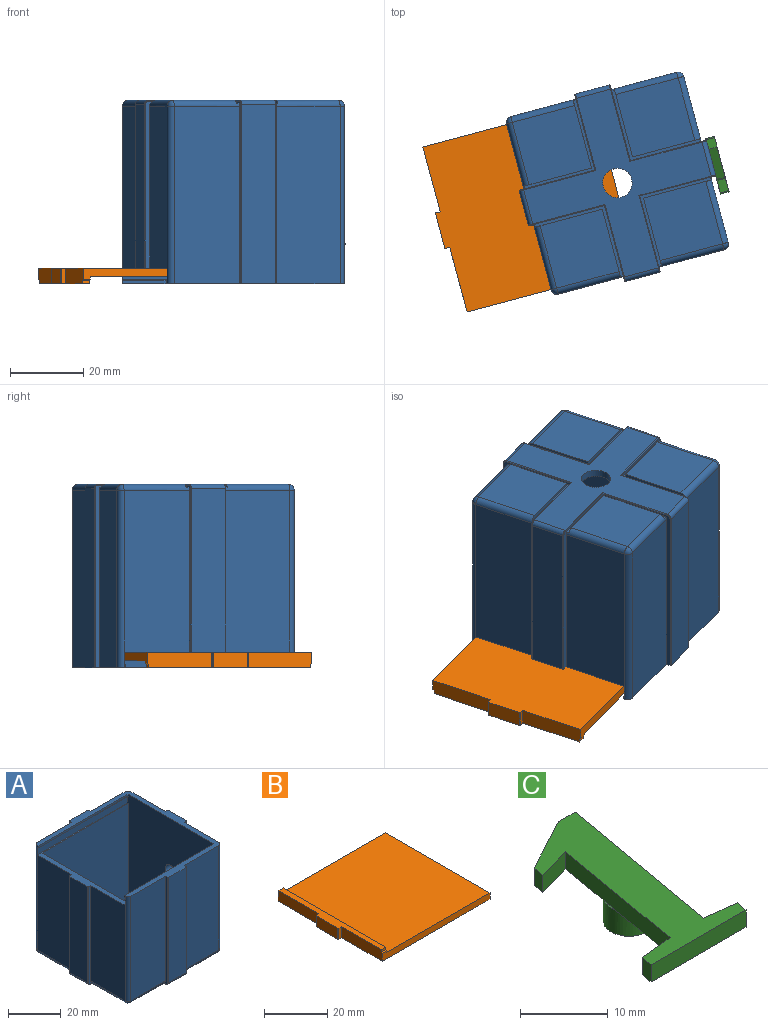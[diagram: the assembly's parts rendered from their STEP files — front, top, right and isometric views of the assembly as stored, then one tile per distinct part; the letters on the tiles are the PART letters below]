
ASSEMBLY  parts=3 mates=2
PART A: 98 faces, bbox 53x53x50.1 mm
  f0: plane 1.27x0.4mm, normal (-1,0,0), area 0.4mm2, adj f6,f33,f62,f95
  f1: plane 1.27x0.4mm, normal (-1,0,0), area 0.4mm2, adj f6,f32,f58,f96
  f2: plane 44.13x18.4mm, normal (-1,0,0), area 812mm2, adj f3,f54,f55,f58
  f3: plane 45.53x21.2mm, normal (0,1,0), area 66.5mm2, adj f2,f30,f38,f54,f55,f73,f75,f76
  f4: plane 44.53x9.6mm, normal (-1,0,0), area 427.5mm2, adj f50,f54,f73,f79
  f5: plane 45.53x21.2mm, normal (0,-1,0), area 66.5mm2, adj f17,f19,f44,f54,f60,f79,f81,f82
  f6: plane 52.8x51.4mm, normal (0,0,1), area 331.8mm2, adj f0,f1,f14,f15,f18,f19,f20,f21
  f7: plane 46x43.73mm, normal (0,-1,0), area 2011.7mm2, adj f8,f34,f35,f54
  f8: plane 46x43.73mm, normal (1,0,0), area 2011.7mm2, adj f7,f9,f35,f54
  f9: plane 46x43.73mm, normal (0,1,0), area 2011.7mm2, adj f8,f34,f35,f54
  f10: plane 17.6x17.6mm, normal (0,0,-1), area 309.8mm2, adj f45,f46,f67,f68
  f11: plane 50.4x50.4mm, normal (0,0,-1), area 825.3mm2, adj f16,f48,f49,f50,f51,f74,f76,f80
  f12: plane 17.6x17.6mm, normal (0,0,-1), area 309.8mm2, adj f42,f43,f59,f60
  f13: plane 17.6x17.6mm, normal (0,0,-1), area 309.8mm2, adj f36,f37,f55,f56
  f14: plane 48.4x18.4mm, normal (1,0,0), area 890.6mm2, adj f6,f26,f68,f70
  f15: plane 48.4x18.4mm, normal (0,1,0), area 890.6mm2, adj f6,f30,f56,f58
  f16: cylinder r=4mm len=8mm, axis (0,0,-1), area 50.3mm2, adj f11,f35
  f17: plane 44.13x18.4mm, normal (-1,0,0), area 812mm2, adj f5,f54,f60,f62
  f18: plane 48.4x18.4mm, normal (0,-1,0), area 890.6mm2, adj f6,f19,f59,f62
  f19: plane 49.8x21.2mm, normal (-1,0,0), area 71.6mm2, adj f5,f6,f18,f44,f59,f77,f78,f80
  f20: plane 48.8x9.6mm, normal (0,-1,0), area 468.5mm2, adj f6,f49,f77,f85
  f21: plane 49.8x21.2mm, normal (1,0,0), area 71.6mm2, adj f6,f22,f24,f41,f64,f85,f87,f88
  f22: plane 48.4x18.4mm, normal (0,-1,0), area 890.6mm2, adj f6,f21,f64,f66
  f23: plane 48.4x18.4mm, normal (1,0,0), area 890.6mm2, adj f6,f24,f63,f66
  f24: plane 49.8x21.2mm, normal (0,-1,0), area 71.6mm2, adj f6,f21,f23,f41,f63,f83,f84,f86
  f25: plane 48.8x9.6mm, normal (1,0,0), area 440.2mm2, adj f6,f48,f83,f89,f97
  f26: plane 49.8x21.2mm, normal (0,1,0), area 71.6mm2, adj f6,f14,f28,f47,f68,f89,f90,f91
  f27: plane 48.4x18.4mm, normal (0,1,0), area 890.6mm2, adj f6,f28,f67,f70
  f28: plane 49.8x21.2mm, normal (1,0,0), area 71.6mm2, adj f6,f26,f27,f47,f67,f92,f93,f94
  f29: plane 48.8x9.6mm, normal (0,1,0), area 468.5mm2, adj f6,f51,f71,f93
  f30: plane 49.8x21.2mm, normal (-1,0,0), area 71.6mm2, adj f3,f6,f15,f38,f56,f71,f72,f74
  f31: plane 17.6x17.6mm, normal (0,0,-1), area 309.8mm2, adj f39,f40,f63,f64
  f32: plane 48x0.87mm, normal (0,-1,0), area 41.7mm2, adj f1,f6,f34,f96
  f33: plane 48x0.87mm, normal (0,1,0), area 41.7mm2, adj f0,f6,f34,f95
  f34: plane 48x46.8mm, normal (-1,0,0), area 2182.3mm2, adj f6,f7,f9,f32,f33,f35,f52,f53
  f35: plane 46x46mm, normal (0,0,1), area 2065.7mm2, adj f7,f8,f9,f16,f34
  f36: plane 18.99x0.8mm, normal (0,-1,0), area 14.9mm2, adj f13,f37,f38,f55
  f37: plane 18.99x0.8mm, normal (1,0,0), area 14.9mm2, adj f13,f36,f38,f56
  f38: plane 19.79x19.79mm, normal (0,0,-1), area 31mm2, adj f3,f30,f36,f37,f55,f56
  f39: plane 18.99x0.8mm, normal (-1,0,0), area 14.9mm2, adj f31,f40,f41,f64
  f40: plane 18.99x0.8mm, normal (0,1,0), area 14.9mm2, adj f31,f39,f41,f63
  f41: plane 19.79x19.79mm, normal (0,0,-1), area 31mm2, adj f21,f24,f39,f40,f63,f64
  f42: plane 18.99x0.8mm, normal (1,0,0), area 14.9mm2, adj f12,f43,f44,f59
  f43: plane 18.99x0.8mm, normal (0,1,0), area 14.9mm2, adj f12,f42,f44,f60
  f44: plane 19.79x19.79mm, normal (0,0,-1), area 31mm2, adj f5,f19,f42,f43,f59,f60
  f45: plane 18.99x0.8mm, normal (0,-1,0), area 14.9mm2, adj f10,f46,f47,f68
  f46: plane 18.99x0.8mm, normal (-1,0,0), area 14.9mm2, adj f10,f45,f47,f67
  f47: plane 19.79x19.79mm, normal (0,0,-1), area 31mm2, adj f26,f28,f45,f46,f67,f68
  f48: cylinder r=1.2mm len=9.6mm, axis (0,1,0), area 18.1mm2, adj f11,f25,f84,f90
  f49: cylinder r=1.2mm len=9.6mm, axis (1,0,0), area 18.1mm2, adj f11,f20,f78,f87
  f50: cylinder r=1.2mm len=9.6mm, axis (0,-1,0), area 18.1mm2, adj f4,f11,f75,f81
  f51: cylinder r=1.2mm len=9.6mm, axis (-1,0,0), area 18.1mm2, adj f11,f29,f72,f94
  f52: plane 48x3mm, normal (0,-1,0), area 144mm2, adj f34,f54,f58,f96
  f53: plane 48x3mm, normal (0,1,0), area 144mm2, adj f34,f54,f62,f95
  f54: plane 49.4x46.8mm, normal (0,0,1), area 144.4mm2, adj f2,f3,f4,f5,f7,f8,f9,f17
  f55: cylinder r=1.6mm len=18.4mm, axis (0,-1,0), area 44.9mm2, adj f2,f3,f13,f36,f38,f57
  f56: cylinder r=1.6mm len=18.4mm, axis (-1,0,0), area 44.9mm2, adj f13,f15,f30,f37,f38,f57
  f57: sphere r=1.6mm, area 4mm2, adj f55,f56,f58
  f58: cylinder r=1.6mm len=48.4mm, axis (0,0,1), area 121.6mm2, adj f1,f2,f6,f15,f52,f57
  f59: cylinder r=1.6mm len=18.4mm, axis (1,0,0), area 44.9mm2, adj f12,f18,f19,f42,f44,f61
  f60: cylinder r=1.6mm len=18.4mm, axis (0,-1,0), area 44.9mm2, adj f5,f12,f17,f43,f44,f61
  f61: sphere r=1.6mm, area 4mm2, adj f59,f60,f62
  f62: cylinder r=1.6mm len=48.4mm, axis (0,0,-1), area 121.6mm2, adj f0,f6,f17,f18,f53,f61
  f63: cylinder r=1.6mm len=18.4mm, axis (0,1,0), area 44.9mm2, adj f23,f24,f31,f40,f41,f65
  f64: cylinder r=1.6mm len=18.4mm, axis (1,0,0), area 44.9mm2, adj f21,f22,f31,f39,f41,f65
  f65: sphere r=1.6mm, area 4mm2, adj f63,f64,f66
  f66: cylinder r=1.6mm len=48.4mm, axis (0,0,1), area 121.6mm2, adj f6,f22,f23,f65
  f67: cylinder r=1.6mm len=18.4mm, axis (-1,0,0), area 44.9mm2, adj f10,f27,f28,f46,f47,f69
  f68: cylinder r=1.6mm len=18.4mm, axis (0,1,0), area 44.9mm2, adj f10,f14,f26,f45,f47,f69
  f69: sphere r=1.6mm, area 4mm2, adj f67,f68,f70
  f70: cylinder r=1.6mm len=48.4mm, axis (0,0,-1), area 121.6mm2, adj f6,f14,f27,f69
  f71: cylinder r=0.2mm len=48.8mm, axis (0,0,1), area 15.3mm2, adj f6,f29,f30,f72
  f72: torus R=1mm, axis (-1,0,0), area 0.6mm2, adj f30,f51,f71,f74
  f73: cylinder r=0.2mm len=44.53mm, axis (0,0,-1), area 14mm2, adj f3,f4,f54,f75
  f74: cylinder r=0.2mm len=20.4mm, axis (0,-1,0), area 6.4mm2, adj f11,f30,f72,f76
  f75: torus R=1mm, axis (0,-1,0), area 0.6mm2, adj f3,f50,f73,f76
  f76: cylinder r=0.2mm len=20.4mm, axis (-1,0,0), area 6.4mm2, adj f3,f11,f74,f75
  f77: cylinder r=0.2mm len=48.8mm, axis (0,0,-1), area 15.3mm2, adj f6,f19,f20,f78
  f78: torus R=1mm, axis (1,0,0), area 0.6mm2, adj f19,f49,f77,f80
  f79: cylinder r=0.2mm len=44.53mm, axis (0,0,1), area 14mm2, adj f4,f5,f54,f81
  f80: cylinder r=0.2mm len=20.4mm, axis (0,-1,0), area 6.4mm2, adj f11,f19,f78,f82
  f81: torus R=1mm, axis (0,-1,0), area 0.6mm2, adj f5,f50,f79,f82
  f82: cylinder r=0.2mm len=20.4mm, axis (1,0,0), area 6.4mm2, adj f5,f11,f80,f81
  f83: cylinder r=0.2mm len=48.8mm, axis (0,0,-1), area 15.3mm2, adj f6,f24,f25,f84
  f84: torus R=1mm, axis (0,1,0), area 0.6mm2, adj f24,f48,f83,f86
  f85: cylinder r=0.2mm len=48.8mm, axis (0,0,1), area 15.3mm2, adj f6,f20,f21,f87
  f86: cylinder r=0.2mm len=20.4mm, axis (1,0,0), area 6.4mm2, adj f11,f24,f84,f88
  f87: torus R=1mm, axis (1,0,0), area 0.6mm2, adj f21,f49,f85,f88
  f88: cylinder r=0.2mm len=20.4mm, axis (0,1,0), area 6.4mm2, adj f11,f21,f86,f87
  f89: cylinder r=0.2mm len=48.8mm, axis (0,0,1), area 15.3mm2, adj f6,f25,f26,f90
  f90: torus R=1mm, axis (0,1,0), area 0.6mm2, adj f26,f48,f89,f91
  f91: cylinder r=0.2mm len=20.4mm, axis (-1,0,0), area 6.4mm2, adj f11,f26,f90,f92
  f92: cylinder r=0.2mm len=20.4mm, axis (0,1,0), area 6.4mm2, adj f11,f28,f91,f94
  f93: cylinder r=0.2mm len=48.8mm, axis (0,0,-1), area 15.3mm2, adj f6,f28,f29,f94
  f94: torus R=1mm, axis (-1,0,0), area 0.6mm2, adj f28,f51,f92,f93
  f95: plane 48x0.4mm, normal (0,0.71,-0.71), area 27.2mm2, adj f0,f33,f34,f53
  f96: plane 48x0.4mm, normal (0,-0.71,-0.71), area 27.2mm2, adj f1,f32,f34,f52
  f97: cylinder r=3mm len=6mm, axis (1,0,0), area 64.1mm2, adj f25,f34
PART B: 18 faces, bbox 49.4x46.5x4.3 mm
  f0: plane 18.25x4.27mm, normal (-1,0,0), area 77.5mm2, adj f3,f4,f7,f10,f12,f17
  f1: plane 18.25x4.27mm, normal (-1,0,0), area 77.5mm2, adj f4,f5,f7,f8,f11,f16
  f2: plane 46.5x46mm, normal (0,0,1), area 2139mm2, adj f3,f5,f6,f9
  f3: plane 48x3mm, normal (0,1,0), area 116.4mm2, adj f0,f2,f4,f6,f9,f17
  f4: plane 49.4x46.5mm, normal (0,0,-1), area 2246mm2, adj f0,f1,f3,f5,f6,f11,f12,f13
  f5: plane 48x3mm, normal (0,-1,0), area 116.4mm2, adj f1,f2,f4,f6,f9,f16
  f6: plane 46.5x2.4mm, normal (1,0,0), area 111.6mm2, adj f2,f3,f4,f5
  f7: plane 45.7x3.4mm, normal (0,0,1), area 105.4mm2, adj f0,f1,f8,f9,f10,f11,f12,f13
  f8: plane 2x0.87mm, normal (0,-1,0), area 1.7mm2, adj f1,f7,f9,f16
  f9: plane 46.5x1.87mm, normal (1,0,0), area 86mm2, adj f2,f3,f5,f7,f8,f10,f16,f17
  f10: plane 2x0.87mm, normal (0,1,0), area 1.7mm2, adj f0,f7,f9,f17
  f11: plane 4.27x1.2mm, normal (0,-1,0), area 5.1mm2, adj f1,f4,f7,f14
  f12: plane 4.27x1.2mm, normal (0,1,0), area 5.1mm2, adj f0,f4,f7,f15
  f13: plane 9.6x4.27mm, normal (-1,0,0), area 41mm2, adj f4,f7,f14,f15
  f14: cylinder r=0.2mm len=4.27mm, axis (0,0,1), area 1.3mm2, adj f4,f7,f11,f13
  f15: cylinder r=0.2mm len=4.27mm, axis (0,0,-1), area 1.3mm2, adj f4,f7,f12,f13
  f16: plane 2x0.4mm, normal (0,-0.71,0.71), area 1.1mm2, adj f1,f5,f8,f9
  f17: plane 2x0.4mm, normal (0,0.71,0.71), area 1.1mm2, adj f0,f3,f9,f10
PART C: 18 faces, bbox 15.6x27.5x5.8 mm
  f0: plane 2.14x0.44mm, normal (0,0,1), area 0.3mm2, adj f2,f6
  f1: plane 2.56x0.57mm, normal (0,0,1), area 0.5mm2, adj f2,f12
  f2: cylinder r=2.95mm len=5.9mm, axis (0,0,1), area 63mm2, adj f0,f1,f3,f4,f5
  f3: plane 5.9x5.9mm, normal (0,0,-1), area 27.3mm2, adj f2
  f4: plane 13.05x11.48mm, normal (0,0,-1), area 72.3mm2, adj f2,f6,f12,f13,f14,f15,f16
  f5: plane 15.64x13.05mm, normal (0,0,-1), area 81.1mm2, adj f2,f6,f7,f8,f9,f10,f11,f12
  f6: plane 20.47x3.6mm, normal (-0.98,0.17,0), area 49.9mm2, adj f0,f4,f5,f7,f16,f17
  f7: plane 5.01x2.4mm, normal (-0.1,1,0), area 12.1mm2, adj f5,f6,f8,f17
  f8: plane 2.4x1.75mm, normal (-0.99,0.17,0), area 4.3mm2, adj f5,f7,f9,f17
  f9: plane 15.34x2.4mm, normal (0,-1,0), area 36.8mm2, adj f5,f8,f10,f17
  f10: plane 2.4x1.75mm, normal (0.99,-0.17,0), area 4.3mm2, adj f5,f9,f11,f17
  f11: plane 4.86x2.4mm, normal (0.1,0.99,0), area 11.7mm2, adj f5,f10,f12,f17
  f12: plane 25.27x4.46mm, normal (0.98,-0.17,0), area 61.6mm2, adj f1,f4,f5,f11,f13,f17
  f13: plane 2.69x2.4mm, normal (0,1,0), area 6.5mm2, adj f4,f12,f14,f17
  f14: plane 8.48x4.52mm, normal (-0.47,0.88,0), area 23.1mm2, adj f4,f13,f15,f17
  f15: plane 2.4x1.73mm, normal (-0.98,0.17,0), area 4.2mm2, adj f4,f14,f16,f17
  f16: plane 5.15x2.4mm, normal (0.27,-0.96,0), area 12.8mm2, adj f4,f6,f15,f17
  f17: plane 27.51x15.64mm, normal (0,0,1), area 180mm2, adj f6,f7,f8,f9,f10,f11,f12,f13
PLACE A rot(axis=(-0.99,-0.13,0),180deg) t=(-48.86,-100.2,172.63)mm
PLACE B rot(axis=(-0.99,-0.13,0),180deg) t=(-71.71,-106.32,172.63)mm
PLACE C rot(axis=(0.48,0.62,0.62),129deg) t=(-35.57,-47.82,62.32)mm
MATE fastened C.f2 <-> A.f97  axis (-0.97,-0.26,0) through (-26.65,-94.25,147.03)mm
MATE slider B.f13 <-> A.f4  axis (-0.97,-0.26,0) through (-97.21,-113.15,126.9)mm
